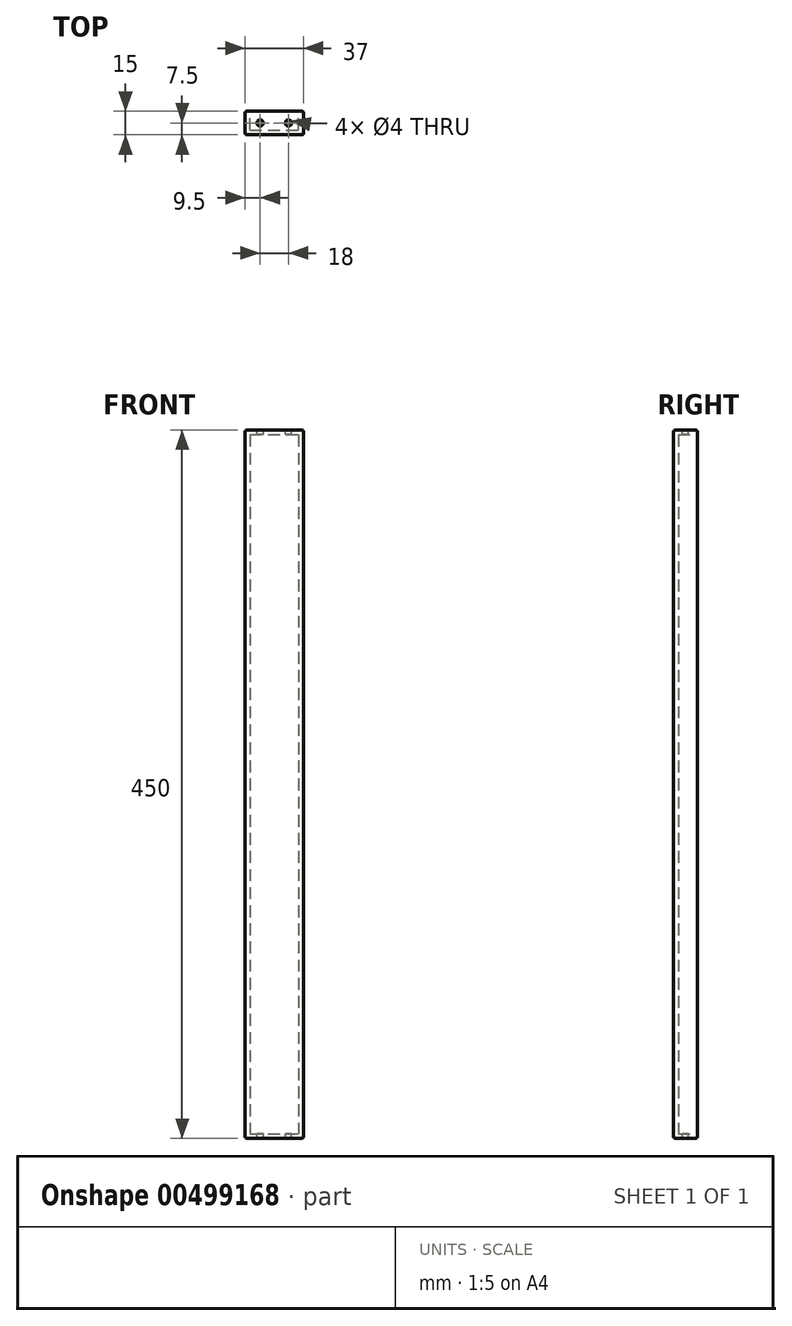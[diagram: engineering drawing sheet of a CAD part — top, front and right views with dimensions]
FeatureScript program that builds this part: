
annotation { "Feature Type Name" : "Feature", "Feature Type Description" : "" }
export const myFeature = defineFeature(function(context is Context, id is Id, definition is map)
    precondition{}
    {
        {
            var Q0;
            Q0=qCreatedBy(makeId("Top.planeOp"),FACE);
            var sketch = newSketch(context, id + "F0", { "sketchPlane" : qUnion([Q0])});
            skLineSegment(sketch, "E0", {"start": v(-25.48, 0) * mm, "end": v(28.63, 0) * mm, "construction": true});
            skLineSegment(sketch, "E1", {"start": v(0, 28.13) * mm, "end": v(0, -28) * mm, "construction": true});
            skLineSegment(sketch, "E2.bottom", {"start": v(-18.5, 7.5) * mm, "end": v(18.5, 7.5) * mm});
            skLineSegment(sketch, "E2.top", {"start": v(-18.5, -7.5) * mm, "end": v(18.5, -7.5) * mm});
            skLineSegment(sketch, "E2.left", {"start": v(-18.5, 7.5) * mm, "end": v(-18.5, -7.5) * mm});
            skLineSegment(sketch, "E2.right", {"start": v(18.5, 7.5) * mm, "end": v(18.5, -7.5) * mm});
            skSolve(sketch);
        }
        {
            var Q0;
            Q0=qSketchRegion(id+"F0",true);
            extrude(context, id + "F1", {"entities" : qUnion([Q0]), "depth" : 450 * mm});
        }
        {
            var Q0;
            Q0=makeQuery(id+"F1.opExtrude","SWEPT_FACE",FACE,{"disambiguationData":[OSD([sQuery(id+"F0.wireOp",EDGE,"E2.bottom")])]});
            var sketch = newSketch(context, id + "F2", { "sketchPlane" : qUnion([Q0])});
            skLineSegment(sketch, "E3.0", {"start": v(-15.5, 447) * mm, "end": v(-15.5, 3) * mm});
            skLineSegment(sketch, "E3.1", {"start": v(15.5, 447) * mm, "end": v(-15.5, 447) * mm});
            skLineSegment(sketch, "E3.2", {"start": v(15.5, 447) * mm, "end": v(15.5, 3) * mm});
            skLineSegment(sketch, "E3.3", {"start": v(15.5, 3) * mm, "end": v(-15.5, 3) * mm});
            skSolve(sketch);
        }
        {
            var Q0;
            Q0=qSketchRegion(id+"F2",true);
            extrude(context, id + "F3", {"entities" : qUnion([Q0]), "operationType" : NewBodyOperationType.REMOVE, "oppositeDirection" : true, "depth" : 12 * mm});
        }
        {
            var Q0;
            Q0=makeQuery(id+"F1.opExtrude","CAP_FACE",FACE,{"disambiguationData":[OSD([sQuery(id+"F0.wireOp",EDGE,"E2.bottom"),sQuery(id+"F0.wireOp",EDGE,"E2.top"),sQuery(id+"F0.wireOp",EDGE,"E2.left"),sQuery(id+"F0.wireOp",EDGE,"E2.right")])],"isStart":false});
            var sketch = newSketch(context, id + "F4", { "sketchPlane" : qUnion([Q0])});
            skLineSegment(sketch, "E4", {"start": v(18.5, 0) * mm, "end": v(-18.5, 0) * mm, "construction": true});
            skLineSegment(sketch, "E5", {"start": v(0, -7.5) * mm, "end": v(0, 7.5) * mm, "construction": true});
            skCircle(sketch, "E6", {"center": v(9, 0) * mm, "radius": 2 * mm});
            skCircle(sketch, "E7", {"center": v(-9, 0) * mm, "radius": 2 * mm});
            skSolve(sketch);
        }
        {
            var Q0;
            Q0=qSketchRegion(id+"F4",true);
            extrude(context, id + "F5", {"entities" : qUnion([Q0]), "operationType" : NewBodyOperationType.REMOVE, "endBound" : BoundingType.THROUGH_ALL, "oppositeDirection" : true, "depth" : 25 * mm});
        }
        {
            var Q0;
            Q0=makeQuery(id+"F1.opExtrude","CAP_EDGE",EDGE,{"disambiguationData":[OSD([sQuery(id+"F0.wireOp",EDGE,"E2.left")])],"isStart":false});
            var Q1;
            Q1=makeQuery(id+"F1.opExtrude","CAP_EDGE",EDGE,{"disambiguationData":[OSD([sQuery(id+"F0.wireOp",EDGE,"E2.right")])],"isStart":false});
            var Q2;
            Q2=makeQuery(id+"F1.opExtrude","CAP_EDGE",EDGE,{"disambiguationData":[OSD([sQuery(id+"F0.wireOp",EDGE,"E2.left")])],"isStart":true});
            var Q3;
            Q3=makeQuery(id+"F1.opExtrude","CAP_EDGE",EDGE,{"disambiguationData":[OSD([sQuery(id+"F0.wireOp",EDGE,"E2.right")])],"isStart":true});
            fillet(context, id + "F6", {"entities" : qUnion([Q0, Q1, Q2, Q3]), "radius" : 1 * mm, "tangentPropagation" : true, "allowEdgeOverflow" : false});
        }
        {
            var Q0;
            Q0=makeQuery(id+"F1.opExtrude","SWEPT_EDGE",EDGE,{"disambiguationData":[OSD([sQuery(id+"F0.wireOp",EDGE,"E2.top"),sQuery(id+"F0.wireOp",EDGE,"E2.right")])]});
            var Q1;
            Q1=makeQuery(id+"F1.opExtrude","SWEPT_EDGE",EDGE,{"disambiguationData":[OSD([sQuery(id+"F0.wireOp",EDGE,"E2.bottom"),sQuery(id+"F0.wireOp",EDGE,"E2.right")])]});
            fillet(context, id + "F7", {"entities" : qUnion([Q0, Q1]), "radius" : 1 * mm, "tangentPropagation" : true, "allowEdgeOverflow" : false});
        }
    });
